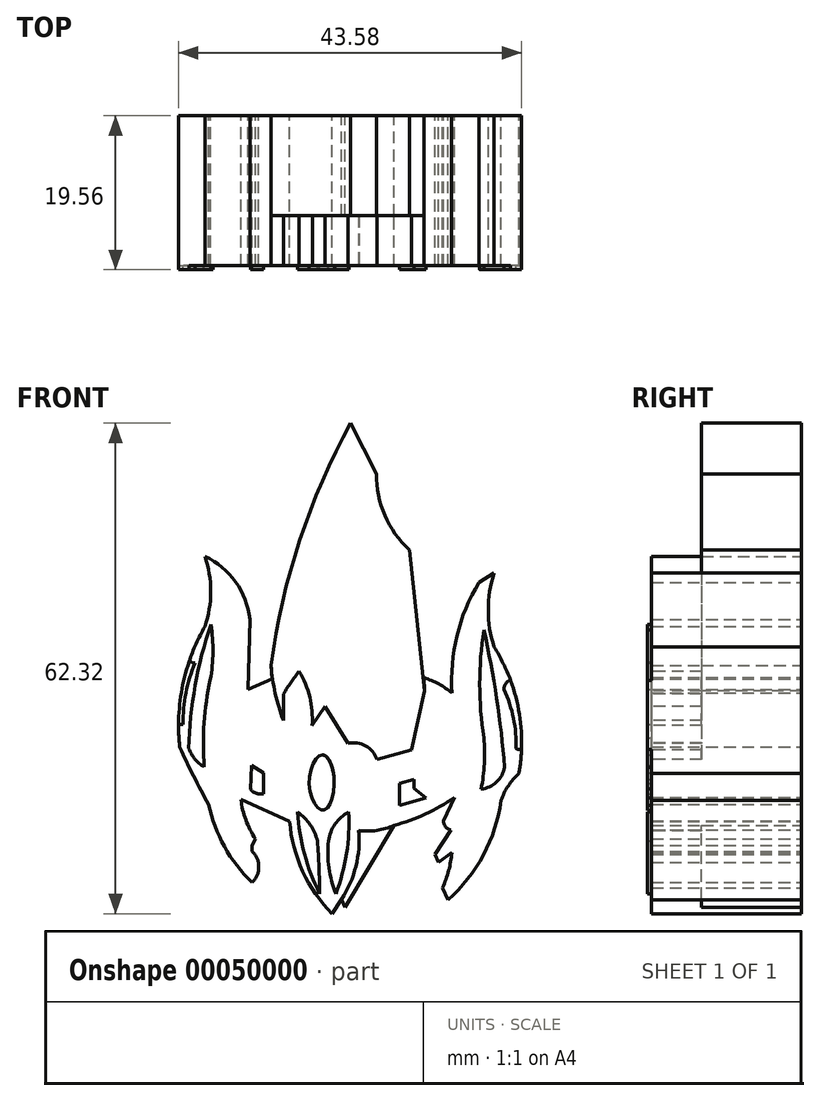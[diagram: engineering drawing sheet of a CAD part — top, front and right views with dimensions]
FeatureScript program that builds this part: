
annotation { "Feature Type Name" : "Feature", "Feature Type Description" : "" }
export const myFeature = defineFeature(function(context is Context, id is Id, definition is map)
    precondition{}
    {
        {
            var Q0;
            Q0=qCreatedBy(makeId("Front.planeOp"),FACE);
            var sketch = newSketch(context, id + "F0", { "sketchPlane" : qUnion([Q0])});
            skPoint(sketch, "E0", {"position": v(26.68, 69.5) * mm});
            skPoint(sketch, "E1", {"position": v(16.56, 38.73) * mm});
            skPoint(sketch, "E2", {"position": v(16.7, 37) * mm});
            skPoint(sketch, "E3", {"position": v(13.63, 35.67) * mm});
            skPoint(sketch, "E4", {"position": v(13.9, 44.59) * mm});
            skPoint(sketch, "E5", {"position": v(8.17, 52.58) * mm});
            skPoint(sketch, "E6", {"position": v(8.17, 43.66) * mm});
            skPoint(sketch, "E7", {"position": v(4.97, 28.34) * mm});
            skPoint(sketch, "E8", {"position": v(14.16, 11.16) * mm});
            skPoint(sketch, "E9", {"position": v(14.16, 15.88) * mm});
            skPoint(sketch, "E10", {"position": v(14.6, 16.68) * mm});
            skPoint(sketch, "E11", {"position": v(12.75, 21.7) * mm});
            skPoint(sketch, "E12", {"position": v(18.93, 18.9) * mm});
            skPoint(sketch, "E13", {"position": v(24.34, 7.17) * mm});
            skPoint(sketch, "E14", {"position": v(25.53, 9) * mm});
            skPoint(sketch, "E15", {"position": v(25.99, 8) * mm});
            skPoint(sketch, "E16", {"position": v(32.2, 18.4) * mm});
            skPoint(sketch, "E17", {"position": v(39.84, 21.94) * mm});
            skPoint(sketch, "E18", {"position": v(38.46, 18.98) * mm});
            skPoint(sketch, "E19", {"position": v(39.42, 17.8) * mm});
            skPoint(sketch, "E20", {"position": v(37.84, 13.73) * mm});
            skPoint(sketch, "E21", {"position": v(39.53, 14.96) * mm});
            skPoint(sketch, "E22", {"position": v(38.34, 10.47) * mm});
            skPoint(sketch, "E23", {"position": v(39.03, 8.93) * mm});
            skPoint(sketch, "E24", {"position": v(45.79, 21.56) * mm});
            skPoint(sketch, "E25", {"position": v(48.05, 24.97) * mm});
            skPoint(sketch, "E26", {"position": v(44.9, 41.05) * mm});
            skPoint(sketch, "E27", {"position": v(44.9, 50.44) * mm});
            skPoint(sketch, "E28", {"position": v(42.97, 49.25) * mm});
            skPoint(sketch, "E29", {"position": v(39.56, 35.2) * mm});
            skPoint(sketch, "E30", {"position": v(36, 37.16) * mm});
            skPoint(sketch, "E31", {"position": v(34.13, 53.39) * mm});
            skPoint(sketch, "E32", {"position": v(31.14, 57.52) * mm});
            skPoint(sketch, "E33", {"position": v(29.95, 63.05) * mm});
            skLineSegment(sketch, "E34", {"start": v(26.68, 69.5) * mm, "end": v(29.95, 63.05) * mm});
            skArc(sketch, "E35", {"start": v(29.95, 63.05) * mm, "mid": v(31.02, 57.78) * mm, "end": v(34.13, 53.39) * mm});
            skArc(sketch, "E36", {"start": v(42.97, 49.25) * mm, "mid": v(40.18, 42.5) * mm, "end": v(39.56, 35.2) * mm});
            skArc(sketch, "E37", {"start": v(44.9, 50.44) * mm, "mid": v(44.15, 45.75) * mm, "end": v(44.9, 41.05) * mm});
            skLineSegment(sketch, "E38", {"start": v(42.97, 49.25) * mm, "end": v(44.9, 50.44) * mm});
            skLineSegment(sketch, "E39", {"start": v(34.13, 53.39) * mm, "end": v(36, 37.16) * mm});
            skArc(sketch, "E40", {"start": v(39.56, 35.2) * mm, "mid": v(37.87, 36.35) * mm, "end": v(36, 37.16) * mm});
            skArc(sketch, "E41", {"start": v(48.05, 24.97) * mm, "mid": v(47.98, 33.3) * mm, "end": v(44.9, 41.05) * mm});
            skArc(sketch, "E42", {"start": v(39.03, 8.93) * mm, "mid": v(43.54, 14.64) * mm, "end": v(45.79, 21.56) * mm});
            skArc(sketch, "E43", {"start": v(48.05, 24.97) * mm, "mid": v(46.7, 23.4) * mm, "end": v(45.79, 21.56) * mm});
            skLineSegment(sketch, "E44", {"start": v(38.34, 10.47) * mm, "end": v(39.03, 8.93) * mm});
            skLineSegment(sketch, "E45", {"start": v(37.84, 13.73) * mm, "end": v(37.4, 14.72) * mm});
            skLineSegment(sketch, "E46", {"start": v(37.4, 14.72) * mm, "end": v(39.42, 17.8) * mm});
            skLineSegment(sketch, "E47", {"start": v(39.53, 14.96) * mm, "end": v(37.84, 13.73) * mm});
            skArc(sketch, "E48", {"start": v(38.34, 10.47) * mm, "mid": v(39.13, 12.66) * mm, "end": v(39.53, 14.96) * mm});
            skArc(sketch, "E49", {"start": v(38.46, 18.98) * mm, "mid": v(38.74, 18.23) * mm, "end": v(39.42, 17.8) * mm});
            skArc(sketch, "E50", {"start": v(32.2, 18.4) * mm, "mid": v(36.17, 19.85) * mm, "end": v(39.84, 21.94) * mm});
            skLineSegment(sketch, "E51", {"start": v(39.84, 21.94) * mm, "end": v(38.46, 18.98) * mm});
            skLineSegment(sketch, "E52", {"start": v(25.99, 8) * mm, "end": v(32.2, 18.4) * mm});
            skLineSegment(sketch, "E53", {"start": v(25.99, 8) * mm, "end": v(25.53, 9) * mm});
            skLineSegment(sketch, "E54", {"start": v(25.53, 9) * mm, "end": v(24.34, 7.17) * mm});
            skArc(sketch, "E55", {"start": v(18.93, 18.9) * mm, "mid": v(20.59, 12.56) * mm, "end": v(24.34, 7.17) * mm});
            skArc(sketch, "E56", {"start": v(12.75, 21.7) * mm, "mid": v(13.36, 19.08) * mm, "end": v(14.6, 16.68) * mm});
            skLineSegment(sketch, "E57", {"start": v(12.75, 21.7) * mm, "end": v(18.93, 18.9) * mm});
            skLineSegment(sketch, "E58", {"start": v(14.6, 16.68) * mm, "end": v(14.16, 15.88) * mm});
            skPoint(sketch, "E59", {"position": v(14.16, 15.1) * mm});
            skArc(sketch, "E60", {"start": v(14.16, 11.16) * mm, "mid": v(15, 13.13) * mm, "end": v(14.16, 15.1) * mm});
            skLineSegment(sketch, "E61", {"start": v(14.16, 15.88) * mm, "end": v(14.16, 15.1) * mm});
            skArc(sketch, "E62", {"start": v(8.64, 21.08) * mm, "mid": v(10.64, 15.7) * mm, "end": v(14.16, 11.16) * mm});
            skArc(sketch, "E63", {"start": v(4.97, 28.34) * mm, "mid": v(6.72, 24.67) * mm, "end": v(8.64, 21.08) * mm});
            skArc(sketch, "E64", {"start": v(8.17, 43.66) * mm, "mid": v(5.35, 36.25) * mm, "end": v(4.97, 28.34) * mm});
            skArc(sketch, "E65", {"start": v(8.17, 43.66) * mm, "mid": v(8.9, 48.12) * mm, "end": v(8.17, 52.58) * mm});
            skArc(sketch, "E66", {"start": v(13.9, 44.59) * mm, "mid": v(12.06, 49.32) * mm, "end": v(8.17, 52.58) * mm});
            skLineSegment(sketch, "E67", {"start": v(13.9, 44.59) * mm, "end": v(13.63, 35.67) * mm});
            skLineSegment(sketch, "E68", {"start": v(16.7, 37) * mm, "end": v(13.63, 35.67) * mm});
            skLineSegment(sketch, "E69", {"start": v(16.56, 38.73) * mm, "end": v(16.7, 37) * mm});
            skArc(sketch, "E70", {"start": v(26.68, 69.5) * mm, "mid": v(20.2, 54.58) * mm, "end": v(16.56, 38.73) * mm});
            skSolve(sketch);
        }
        {
            var Q0;
            Q0 = qSketchRegion(id + "F0", true);
            extrude(context, id + "F1", {"entities" : qUnion([Q0]), "depth" : 19.05 * mm});
        }
        {
            var Q0;
            Q0=makeQuery(id+"F1.opExtrude","CAP_FACE",FACE,{"disambiguationData":[OSD([sQuery(id+"F0.wireOp",EDGE,"E34"),sQuery(id+"F0.wireOp",EDGE,"E35"),sQuery(id+"F0.wireOp",EDGE,"E36"),sQuery(id+"F0.wireOp",EDGE,"E37"),sQuery(id+"F0.wireOp",EDGE,"E38"),sQuery(id+"F0.wireOp",EDGE,"E39"),sQuery(id+"F0.wireOp",EDGE,"E40"),sQuery(id+"F0.wireOp",EDGE,"E41"),sQuery(id+"F0.wireOp",EDGE,"E42"),sQuery(id+"F0.wireOp",EDGE,"E43"),sQuery(id+"F0.wireOp",EDGE,"E44"),sQuery(id+"F0.wireOp",EDGE,"E45"),sQuery(id+"F0.wireOp",EDGE,"E46"),sQuery(id+"F0.wireOp",EDGE,"E47"),sQuery(id+"F0.wireOp",EDGE,"E48"),sQuery(id+"F0.wireOp",EDGE,"E49"),sQuery(id+"F0.wireOp",EDGE,"E50"),sQuery(id+"F0.wireOp",EDGE,"E51"),sQuery(id+"F0.wireOp",EDGE,"E52"),sQuery(id+"F0.wireOp",EDGE,"E53"),sQuery(id+"F0.wireOp",EDGE,"E54"),sQuery(id+"F0.wireOp",EDGE,"E55"),sQuery(id+"F0.wireOp",EDGE,"E56"),sQuery(id+"F0.wireOp",EDGE,"E57"),sQuery(id+"F0.wireOp",EDGE,"E58"),sQuery(id+"F0.wireOp",EDGE,"E60"),sQuery(id+"F0.wireOp",EDGE,"E61"),sQuery(id+"F0.wireOp",EDGE,"E62"),sQuery(id+"F0.wireOp",EDGE,"E63"),sQuery(id+"F0.wireOp",EDGE,"E64"),sQuery(id+"F0.wireOp",EDGE,"E65"),sQuery(id+"F0.wireOp",EDGE,"E66"),sQuery(id+"F0.wireOp",EDGE,"E67"),sQuery(id+"F0.wireOp",EDGE,"E68"),sQuery(id+"F0.wireOp",EDGE,"E69"),sQuery(id+"F0.wireOp",EDGE,"E70")])],"isStart":false});
            var sketch = newSketch(context, id + "F2", { "sketchPlane" : qUnion([Q0])});
            skPoint(sketch, "E71", {"position": v(18.15, 31.7) * mm});
            skPoint(sketch, "E72", {"position": v(18.15, 35.09) * mm});
            skPoint(sketch, "E73", {"position": v(20.13, 37.98) * mm});
            skPoint(sketch, "E74", {"position": v(21.78, 31.13) * mm});
            skPoint(sketch, "E75", {"position": v(23.43, 33.52) * mm});
            skPoint(sketch, "E76", {"position": v(26.32, 28.82) * mm});
            skPoint(sketch, "E77", {"position": v(30.03, 26.75) * mm});
            skPoint(sketch, "E78", {"position": v(34.4, 28) * mm});
            skPoint(sketch, "E79", {"position": v(36.06, 35.5) * mm});
            skLineSegment(sketch, "E80", {"start": v(34.13, 53.39) * mm, "end": v(36.06, 35.5) * mm});
            skLineSegment(sketch, "E81", {"start": v(36.06, 35.5) * mm, "end": v(34.4, 28) * mm});
            skLineSegment(sketch, "E82", {"start": v(34.4, 28) * mm, "end": v(30.03, 26.75) * mm});
            skArc(sketch, "E83", {"start": v(30.03, 26.75) * mm, "mid": v(28.57, 28.5) * mm, "end": v(26.32, 28.82) * mm});
            skArc(sketch, "E84", {"start": v(20.13, 37.98) * mm, "mid": v(19.1, 36.57) * mm, "end": v(18.15, 35.09) * mm});
            skArc(sketch, "E85", {"start": v(16.56, 38.73) * mm, "mid": v(17.1, 35.16) * mm, "end": v(18.15, 31.7) * mm});
            skLineSegment(sketch, "E86", {"start": v(18.15, 35.09) * mm, "end": v(18.15, 31.7) * mm});
            skLineSegment(sketch, "E87", {"start": v(23.43, 33.52) * mm, "end": v(21.78, 31.13) * mm});
            skLineSegment(sketch, "E88", {"start": v(23.43, 33.52) * mm, "end": v(26.32, 28.82) * mm});
            skArc(sketch, "E89", {"start": v(21.78, 31.13) * mm, "mid": v(21.49, 34.68) * mm, "end": v(20.13, 37.98) * mm});
            skPoint(sketch, "E90", {"position": v(20.2, 54.58) * mm});
            skArc(sketch, "E91", {"start": v(26.68, 69.5) * mm, "mid": v(20.2, 54.58) * mm, "end": v(16.56, 38.73) * mm});
            skPoint(sketch, "E92", {"position": v(31.02, 57.78) * mm});
            skLineSegment(sketch, "E93", {"start": v(26.68, 69.5) * mm, "end": v(29.95, 63.05) * mm});
            skArc(sketch, "E94", {"start": v(29.95, 63.05) * mm, "mid": v(31.02, 57.78) * mm, "end": v(34.13, 53.39) * mm});
            skPoint(sketch, "E95", {"position": v(27.7, 17.77) * mm});
            skPoint(sketch, "E96", {"position": v(32.2, 18.4) * mm});
            skPoint(sketch, "E97", {"position": v(25.99, 8) * mm});
            skPoint(sketch, "E98", {"position": v(25.53, 9) * mm});
            skArc(sketch, "E99", {"start": v(25.53, 9) * mm, "mid": v(27.34, 13.2) * mm, "end": v(27.7, 17.77) * mm});
            skArc(sketch, "E100", {"start": v(27.7, 17.77) * mm, "mid": v(30, 17.76) * mm, "end": v(32.2, 18.4) * mm});
            skLineSegment(sketch, "E101", {"start": v(25.53, 9) * mm, "end": v(25.99, 8) * mm});
            skLineSegment(sketch, "E102", {"start": v(32.2, 18.4) * mm, "end": v(25.99, 8) * mm});
            skSolve(sketch);
        }
        {
            var Q0;
            Q0 = qSketchRegion(id + "F2", true);
            extrude(context, id + "F3", {"entities" : qUnion([Q0]), "operationType" : NewBodyOperationType.REMOVE, "oppositeDirection" : true, "depth" : 6.35 * mm});
        }
        {
            var Q0;
            Q0=makeQuery(id+"F1.opExtrude","CAP_FACE",FACE,{"disambiguationData":[OSD([sQuery(id+"F0.wireOp",EDGE,"E34"),sQuery(id+"F0.wireOp",EDGE,"E35"),sQuery(id+"F0.wireOp",EDGE,"E36"),sQuery(id+"F0.wireOp",EDGE,"E37"),sQuery(id+"F0.wireOp",EDGE,"E38"),sQuery(id+"F0.wireOp",EDGE,"E39"),sQuery(id+"F0.wireOp",EDGE,"E40"),sQuery(id+"F0.wireOp",EDGE,"E41"),sQuery(id+"F0.wireOp",EDGE,"E42"),sQuery(id+"F0.wireOp",EDGE,"E43"),sQuery(id+"F0.wireOp",EDGE,"E44"),sQuery(id+"F0.wireOp",EDGE,"E45"),sQuery(id+"F0.wireOp",EDGE,"E46"),sQuery(id+"F0.wireOp",EDGE,"E47"),sQuery(id+"F0.wireOp",EDGE,"E48"),sQuery(id+"F0.wireOp",EDGE,"E49"),sQuery(id+"F0.wireOp",EDGE,"E50"),sQuery(id+"F0.wireOp",EDGE,"E51"),sQuery(id+"F0.wireOp",EDGE,"E52"),sQuery(id+"F0.wireOp",EDGE,"E53"),sQuery(id+"F0.wireOp",EDGE,"E54"),sQuery(id+"F0.wireOp",EDGE,"E55"),sQuery(id+"F0.wireOp",EDGE,"E56"),sQuery(id+"F0.wireOp",EDGE,"E57"),sQuery(id+"F0.wireOp",EDGE,"E58"),sQuery(id+"F0.wireOp",EDGE,"E60"),sQuery(id+"F0.wireOp",EDGE,"E61"),sQuery(id+"F0.wireOp",EDGE,"E62"),sQuery(id+"F0.wireOp",EDGE,"E63"),sQuery(id+"F0.wireOp",EDGE,"E64"),sQuery(id+"F0.wireOp",EDGE,"E65"),sQuery(id+"F0.wireOp",EDGE,"E66"),sQuery(id+"F0.wireOp",EDGE,"E67"),sQuery(id+"F0.wireOp",EDGE,"E68"),sQuery(id+"F0.wireOp",EDGE,"E69"),sQuery(id+"F0.wireOp",EDGE,"E70")])],"isStart":false});
            var sketch = newSketch(context, id + "F4", { "sketchPlane" : qUnion([Q0])});
            skPoint(sketch, "E103", {"position": v(46.24, 25.78) * mm});
            skPoint(sketch, "E104", {"position": v(43.25, 23) * mm});
            skPoint(sketch, "E105", {"position": v(43.6, 43.2) * mm});
            skArc(sketch, "E106", {"start": v(43.6, 43.2) * mm, "mid": v(43.07, 36.36) * mm, "end": v(43.6, 29.52) * mm});
            skArc(sketch, "E107", {"start": v(46.24, 25.78) * mm, "mid": v(45.22, 34.54) * mm, "end": v(43.6, 43.2) * mm});
            skArc(sketch, "E108", {"start": v(43.25, 23) * mm, "mid": v(43.67, 26.25) * mm, "end": v(43.6, 29.52) * mm});
            skArc(sketch, "E109", {"start": v(43.25, 23) * mm, "mid": v(45.2, 23.9) * mm, "end": v(46.24, 25.78) * mm});
            skPoint(sketch, "E110", {"position": v(23.1, 27.37) * mm});
            skPoint(sketch, "E111", {"position": v(23.14, 20.32) * mm});
            skPoint(sketch, "E112", {"position": v(24.6, 23.83) * mm});
            skPoint(sketch, "E113", {"position": v(21.4, 23.83) * mm});
            skFitSpline(sketch, "E114", {"points": [v(23.1, 27.37) * mm, v(21.4, 23.83) * mm, v(23.14, 20.32) * mm, v(24.6, 23.83) * mm, v(23.1, 27.37) * mm]});
            skPoint(sketch, "E115", {"position": v(22.46, 16.41) * mm});
            skPoint(sketch, "E116", {"position": v(23.85, 16.41) * mm});
            skPoint(sketch, "E117", {"position": v(26.42, 20.1) * mm});
            skPoint(sketch, "E118", {"position": v(19.94, 20.1) * mm});
            skPoint(sketch, "E119", {"position": v(24.8, 9.71) * mm});
            skPoint(sketch, "E120", {"position": v(22.73, 9.71) * mm});
            skArc(sketch, "E121", {"start": v(23.85, 16.41) * mm, "mid": v(23.92, 13) * mm, "end": v(24.8, 9.71) * mm});
            skArc(sketch, "E122", {"start": v(26.42, 20.1) * mm, "mid": v(24.7, 18.56) * mm, "end": v(23.85, 16.41) * mm});
            skArc(sketch, "E123", {"start": v(24.8, 9.71) * mm, "mid": v(26.15, 14.82) * mm, "end": v(26.42, 20.1) * mm});
            skArc(sketch, "E124", {"start": v(19.94, 20.1) * mm, "mid": v(20.8, 14.76) * mm, "end": v(22.73, 9.71) * mm});
            skArc(sketch, "E125", {"start": v(22.46, 16.41) * mm, "mid": v(21.53, 18.48) * mm, "end": v(19.94, 20.1) * mm});
            skArc(sketch, "E126", {"start": v(22.73, 9.71) * mm, "mid": v(22.65, 13.06) * mm, "end": v(22.46, 16.41) * mm});
            skPoint(sketch, "E127", {"position": v(47.7, 28.15) * mm});
            skPoint(sketch, "E128", {"position": v(47.9, 33.73) * mm});
            skPoint(sketch, "E129", {"position": v(46.99, 36.83) * mm});
            skPoint(sketch, "E130", {"position": v(48.38, 28.07) * mm});
            skPoint(sketch, "E131", {"position": v(46.15, 35.66) * mm});
            skArc(sketch, "E132", {"start": v(48.38, 28.07) * mm, "mid": v(48.12, 32.52) * mm, "end": v(46.99, 36.83) * mm});
            skArc(sketch, "E133", {"start": v(47.7, 28.15) * mm, "mid": v(47.36, 32) * mm, "end": v(46.15, 35.66) * mm});
            skArc(sketch, "E134", {"start": v(46.99, 36.83) * mm, "mid": v(46.37, 36.38) * mm, "end": v(46.15, 35.66) * mm});
            skArc(sketch, "E135", {"start": v(47.7, 28.15) * mm, "mid": v(48.03, 28.02) * mm, "end": v(48.38, 28.07) * mm});
            skArc(sketch, "E136", {"start": v(6.11, 28.18) * mm, "mid": v(6.88, 26.83) * mm, "end": v(8.07, 25.84) * mm});
            skArc(sketch, "E137", {"start": v(8.91, 43.9) * mm, "mid": v(6.92, 36.15) * mm, "end": v(6.11, 28.18) * mm});
            skArc(sketch, "E138", {"start": v(8.84, 36.9) * mm, "mid": v(8.05, 31.4) * mm, "end": v(8.07, 25.84) * mm});
            skArc(sketch, "E139", {"start": v(8.84, 36.9) * mm, "mid": v(9.19, 40.4) * mm, "end": v(8.91, 43.9) * mm});
            skArc(sketch, "E140", {"start": v(6.93, 39.03) * mm, "mid": v(5.74, 35.22) * mm, "end": v(5.4, 31.24) * mm});
            skPoint(sketch, "E141", {"position": v(6.15, 39.19) * mm});
            skPoint(sketch, "E142", {"position": v(4.82, 31.25) * mm});
            skPoint(sketch, "E143", {"position": v(5.2, 35.4) * mm});
            skArc(sketch, "E144", {"start": v(6.15, 39.19) * mm, "mid": v(5.17, 35.27) * mm, "end": v(4.82, 31.25) * mm});
            skLineSegment(sketch, "E145", {"start": v(6.15, 39.19) * mm, "end": v(6.93, 39.03) * mm});
            skLineSegment(sketch, "E146", {"start": v(4.82, 31.25) * mm, "end": v(5.4, 31.24) * mm});
            skPoint(sketch, "E147", {"position": v(32.86, 23.7) * mm});
            skPoint(sketch, "E148", {"position": v(32.86, 20.9) * mm});
            skPoint(sketch, "E149", {"position": v(36.22, 21.88) * mm});
            skPoint(sketch, "E150", {"position": v(34.7, 23.07) * mm});
            skPoint(sketch, "E151", {"position": v(34.7, 24.26) * mm});
            skLineSegment(sketch, "E152", {"start": v(36.22, 21.88) * mm, "end": v(32.86, 20.9) * mm});
            skLineSegment(sketch, "E153", {"start": v(32.86, 23.7) * mm, "end": v(32.86, 20.9) * mm});
            skLineSegment(sketch, "E154", {"start": v(34.7, 24.26) * mm, "end": v(32.86, 23.7) * mm});
            skLineSegment(sketch, "E155", {"start": v(34.7, 23.07) * mm, "end": v(36.22, 21.88) * mm});
            skLineSegment(sketch, "E156", {"start": v(34.7, 24.26) * mm, "end": v(34.7, 23.07) * mm});
            skPoint(sketch, "E157", {"position": v(15.6, 25.09) * mm});
            skPoint(sketch, "E158", {"position": v(14.1, 26.03) * mm});
            skPoint(sketch, "E159", {"position": v(13.96, 22.98) * mm});
            skPoint(sketch, "E160", {"position": v(15.6, 22.4) * mm});
            skArc(sketch, "E161", {"start": v(13.96, 22.98) * mm, "mid": v(14.7, 22.47) * mm, "end": v(15.6, 22.4) * mm});
            skLineSegment(sketch, "E162", {"start": v(14.1, 26.03) * mm, "end": v(15.6, 25.09) * mm});
            skLineSegment(sketch, "E163", {"start": v(14.1, 26.03) * mm, "end": v(13.96, 22.98) * mm});
            skLineSegment(sketch, "E164", {"start": v(15.6, 25.09) * mm, "end": v(15.6, 22.4) * mm});
            skSolve(sketch);
        }
        {
            var Q0;
            Q0 = qSketchRegion(id + "F4", true);
            extrude(context, id + "F5", {"entities" : qUnion([Q0]), "operationType" : NewBodyOperationType.ADD, "depth" : 0.5 * mm});
        }
        {
            var Q0;
            Q0=makeQuery(id+"F1.opExtrude","CAP_FACE",FACE,{"disambiguationData":[OSD([sQuery(id+"F0.wireOp",EDGE,"E34"),sQuery(id+"F0.wireOp",EDGE,"E35"),sQuery(id+"F0.wireOp",EDGE,"E36"),sQuery(id+"F0.wireOp",EDGE,"E37"),sQuery(id+"F0.wireOp",EDGE,"E38"),sQuery(id+"F0.wireOp",EDGE,"E39"),sQuery(id+"F0.wireOp",EDGE,"E40"),sQuery(id+"F0.wireOp",EDGE,"E41"),sQuery(id+"F0.wireOp",EDGE,"E42"),sQuery(id+"F0.wireOp",EDGE,"E43"),sQuery(id+"F0.wireOp",EDGE,"E44"),sQuery(id+"F0.wireOp",EDGE,"E45"),sQuery(id+"F0.wireOp",EDGE,"E46"),sQuery(id+"F0.wireOp",EDGE,"E47"),sQuery(id+"F0.wireOp",EDGE,"E48"),sQuery(id+"F0.wireOp",EDGE,"E49"),sQuery(id+"F0.wireOp",EDGE,"E50"),sQuery(id+"F0.wireOp",EDGE,"E51"),sQuery(id+"F0.wireOp",EDGE,"E52"),sQuery(id+"F0.wireOp",EDGE,"E53"),sQuery(id+"F0.wireOp",EDGE,"E54"),sQuery(id+"F0.wireOp",EDGE,"E55"),sQuery(id+"F0.wireOp",EDGE,"E56"),sQuery(id+"F0.wireOp",EDGE,"E57"),sQuery(id+"F0.wireOp",EDGE,"E58"),sQuery(id+"F0.wireOp",EDGE,"E60"),sQuery(id+"F0.wireOp",EDGE,"E61"),sQuery(id+"F0.wireOp",EDGE,"E62"),sQuery(id+"F0.wireOp",EDGE,"E63"),sQuery(id+"F0.wireOp",EDGE,"E64"),sQuery(id+"F0.wireOp",EDGE,"E65"),sQuery(id+"F0.wireOp",EDGE,"E66"),sQuery(id+"F0.wireOp",EDGE,"E67"),sQuery(id+"F0.wireOp",EDGE,"E68"),sQuery(id+"F0.wireOp",EDGE,"E69"),sQuery(id+"F0.wireOp",EDGE,"E70")])],"isStart":false});
            var sketch = newSketch(context, id + "F6", { "sketchPlane" : qUnion([Q0])});
            skLineSegment(sketch, "E165", {"start": v(36, 37.16) * mm, "end": v(36.06, 35.5) * mm});
            skLineSegment(sketch, "E166", {"start": v(36.06, 35.5) * mm, "end": v(34.13, 53.39) * mm});
            skLineSegment(sketch, "E167", {"start": v(34.13, 53.39) * mm, "end": v(36, 37.16) * mm});
            skSolve(sketch);
        }
        {
            var Q0;
            Q0 = qSketchRegion(id + "F6", true);
            extrude(context, id + "F7", {"entities" : qUnion([Q0]), "operationType" : NewBodyOperationType.REMOVE, "endBound" : BoundingType.UP_TO_NEXT, "oppositeDirection" : true, "depth" : 25.4 * mm});
        }
    });
